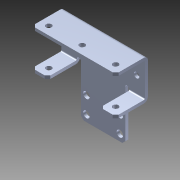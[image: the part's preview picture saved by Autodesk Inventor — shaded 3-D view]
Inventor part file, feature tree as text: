
AUTODESK INVENTOR PART (.ipt)
format: ipt  version: 2014 (Build 180170000, 170)  size: 178,688 bytes
history: native  units: in
note: dims shown in document units (in); Inventor stores cm internally (conversion verified against a paired STEP export)
features: chamfer x1, other x1, imported_body x1
ambient origin geometry x8: Origin, YZ Plane, XZ Plane, XY Plane, X Axis, Y Axis, Z Axis, Center Point
bodies: Body1 (feature_tree)
feature tree (3):
  chamfer  "Chamfer1"  [1 undecoded]
  other  "217-3558-STEP1"
  imported_body  "Base1"
note: 1 required parameter value undecoded (feature->parameter linkage not recoverable at this tier; creation-order binding heuristic only, values carry confidence <= 0.55)
